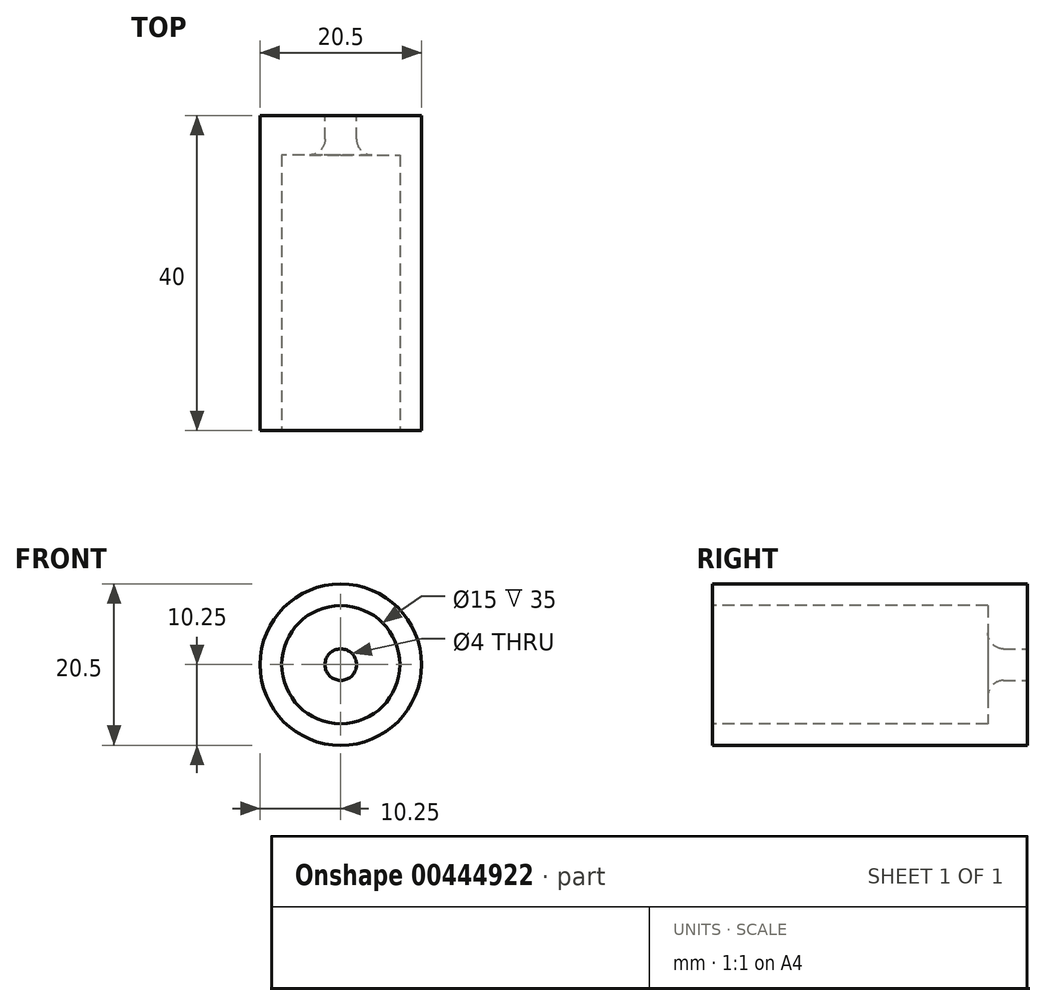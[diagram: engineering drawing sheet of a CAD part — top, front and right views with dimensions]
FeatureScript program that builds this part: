
annotation { "Feature Type Name" : "Feature", "Feature Type Description" : "" }
export const myFeature = defineFeature(function(context is Context, id is Id, definition is map)
    precondition{}
    {
        {
            var Q0;
            Q0=qCreatedBy(makeId("Front.planeOp"),FACE);
            var sketch = newSketch(context, id + "F0", { "sketchPlane" : qUnion([Q0])});
            skCircle(sketch, "E0", {"center": v(0, 0) * mm, "radius": 7.5 * mm});
            skCircle(sketch, "E1", {"center": v(0, 0) * mm, "radius": 10.25 * mm});
            skSolve(sketch);
        }
        {
            var Q0;
            Q0 = qSketchRegion(id + "F0", true);
            extrude(context, id + "F1", {"entities" : qUnion([Q0]), "oppositeDirection" : true, "depth" : 40 * mm});
        }
        {
            var Q0;
            Q0=makeQuery(id+"F1.opExtrude","CAP_FACE",FACE,{"disambiguationData":[OSD([sQuery(id+"F0.wireOp",EDGE,"E0"),sQuery(id+"F0.wireOp",EDGE,"E1")])],"isStart":false});
            var sketch = newSketch(context, id + "F2", { "sketchPlane" : qUnion([Q0])});
            skCircle(sketch, "E2", {"center": v(0, 0) * mm, "radius": 10.25 * mm});
            skCircle(sketch, "E3", {"center": v(0, 0) * mm, "radius": 2 * mm});
            skSolve(sketch);
        }
        {
            var Q0;
            Q0=makeQuery(id+"F2.imprint","IMPRINT",FACE,{"disambiguationData":[TD([[makeQuery(id+"F2.imprint","IMPRINT",EDGE,{"derivedFrom":sQuery(id+"F2.wireOp",EDGE,"E2")}),-1.0]])]});
            var Q1;
            Q1=makeQuery(id+"F2.imprint","IMPRINT",FACE,{"disambiguationData":[TD([[makeQuery(id+"F2.imprint","IMPRINT",EDGE,{"derivedFrom":makeQuery(id+"F1.opExtrude","CAP_EDGE",EDGE,{"disambiguationData":[OSD([sQuery(id+"F0.wireOp",EDGE,"E0")])],"isStart":false})}),-1.0]])]});
            extrude(context, id + "F3", {"entities" : qUnion([Q0, Q1]), "operationType" : NewBodyOperationType.ADD, "oppositeDirection" : true, "depth" : 5 * mm});
        }
        {
            var Q0;
            Q0=makeQuery(id+"F3.opExtrude","CAP_EDGE",EDGE,{"disambiguationData":[OSD([sQuery(id+"F2.wireOp",EDGE,"E3")])],"isStart":false});
            fillet(context, id + "F4", {"entities" : qUnion([Q0]), "radius" : 2 * mm, "tangentPropagation" : true, "allowEdgeOverflow" : false});
        }
    });
